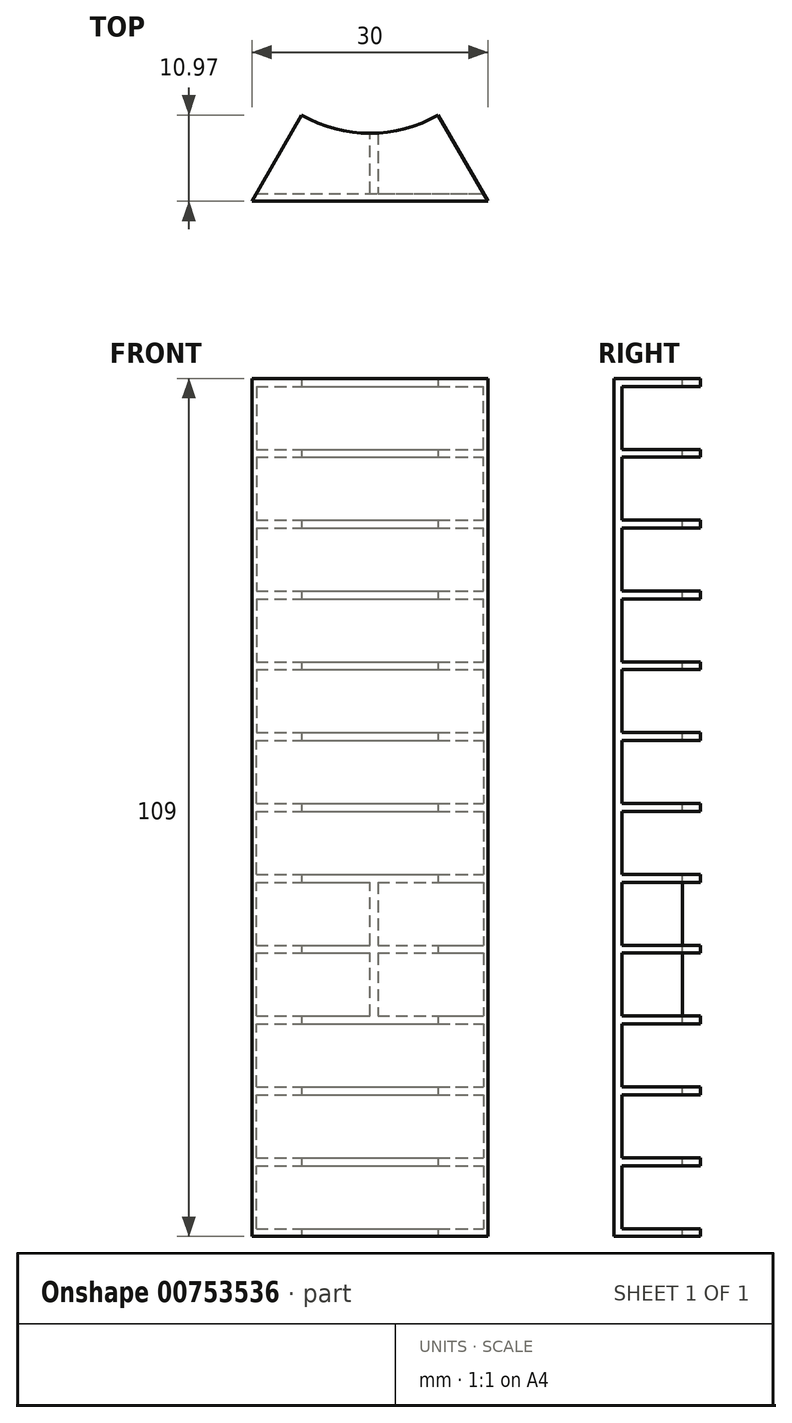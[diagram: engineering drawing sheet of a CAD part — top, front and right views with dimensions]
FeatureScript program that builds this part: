
annotation { "Feature Type Name" : "Feature", "Feature Type Description" : "" }
export const myFeature = defineFeature(function(context is Context, id is Id, definition is map)
    precondition{}
    {
        {
            var Q0;
            Q0=qCreatedBy(makeId("Top.planeOp"),FACE);
            var sketch = newSketch(context, id + "F0", { "sketchPlane" : qUnion([Q0])});
            skCircle(sketch, "E0", {"center": v(0, 0) * mm, "radius": 30 * mm});
            skCircle(sketch, "E1.cCircle", {"center": v(0, 0) * mm, "radius": 30 * mm, "construction": true});
            skLineSegment(sketch, "E1.0", {"start": v(30, 0) * mm, "end": v(15, -25.98) * mm});
            skLineSegment(sketch, "E1.1", {"start": v(15, -25.98) * mm, "end": v(-15, -25.98) * mm});
            skLineSegment(sketch, "E1.2", {"start": v(-15, -25.98) * mm, "end": v(-30, 0) * mm});
            skLineSegment(sketch, "E1.3", {"start": v(-30, 0) * mm, "end": v(-15, 25.98) * mm});
            skLineSegment(sketch, "E1.4", {"start": v(-15, 25.98) * mm, "end": v(15, 25.98) * mm});
            skLineSegment(sketch, "E1.5", {"start": v(15, 25.98) * mm, "end": v(30, 0) * mm});
            skLineSegment(sketch, "E2", {"start": v(-30, 0) * mm, "end": v(30, 0) * mm});
            skLineSegment(sketch, "E3", {"start": v(-15, 25.98) * mm, "end": v(15, -25.98) * mm});
            skLineSegment(sketch, "E4", {"start": v(-15, -25.98) * mm, "end": v(15, 25.98) * mm});
            skCircle(sketch, "E5", {"center": v(0, 0) * mm, "radius": 17.33 * mm});
            skLineSegment(sketch, "E6.0", {"start": v(30, 17.32) * mm, "end": v(30, -17.32) * mm, "construction": true});
            skLineSegment(sketch, "E6.1", {"start": v(30, -17.32) * mm, "end": v(0, -34.64) * mm, "construction": true});
            skLineSegment(sketch, "E6.2", {"start": v(0, -34.64) * mm, "end": v(-30, -17.32) * mm, "construction": true});
            skLineSegment(sketch, "E6.3", {"start": v(-30, -17.32) * mm, "end": v(-30, 17.32) * mm, "construction": true});
            skLineSegment(sketch, "E6.4", {"start": v(-30, 17.32) * mm, "end": v(0, 34.64) * mm, "construction": true});
            skLineSegment(sketch, "E6.5", {"start": v(0, 34.64) * mm, "end": v(30, 17.32) * mm, "construction": true});
            skPoint(sketch, "E6.0.midPoint", {"position": v(30, 0) * mm});
            skLineSegment(sketch, "E7", {"start": v(-30, 17.32) * mm, "end": v(30, -17.32) * mm});
            skLineSegment(sketch, "E8", {"start": v(-30, -17.32) * mm, "end": v(30, 17.32) * mm});
            skLineSegment(sketch, "E9", {"start": v(0, 34.64) * mm, "end": v(0, -34.64) * mm});
            skLineSegment(sketch, "E10", {"start": v(-15, 25.98) * mm, "end": v(55.88, 25.98) * mm, "construction": true});
            skLineSegment(sketch, "E11.0", {"start": v(-14.13, -26.48) * mm, "end": v(15.87, 25.48) * mm});
            skLineSegment(sketch, "E12.0", {"start": v(1, 34.64) * mm, "end": v(1, -34.64) * mm});
            skLineSegment(sketch, "E13", {"start": v(15, -8.67) * mm, "end": v(17.33, 0) * mm});
            skLineSegment(sketch, "E14", {"start": v(-7.78, -15.48) * mm, "end": v(0, -17.33) * mm});
            skSolve(sketch);
        }
        {
            var Q0;
            {var subQ0=sQuery(id+"F0.wireOp",EDGE,"E4");var subQ5=sQuery(id+"F0.wireOp",EDGE,"E5");var subQ6=makeQuery(id+"F0.imprint","INTERSECT",VERTEX,{"disambiguationData":[OD(0.0)],"derivedFrom":[subQ0,subQ5]});Q0=makeQuery(id+"F0.imprint","IMPRINT",FACE,{"disambiguationData":[TD([[makeQuery(id+"F0.imprint","IMPRINT",EDGE,{"disambiguationData":[TD([[subQ6,-1.0]])],"derivedFrom":subQ5}),-1.0]])]});}
            var Q1;
            {var subQ0=sQuery(id+"F0.wireOp",EDGE,"E9");var subQ1=sQuery(id+"F0.wireOp",EDGE,"E1.1");var subQ2=makeQuery(id+"F0.imprint","INTERSECT",VERTEX,{"derivedFrom":[subQ1,subQ0]});Q1=makeQuery(id+"F0.imprint","IMPRINT",FACE,{"disambiguationData":[TD([[makeQuery(id+"F0.imprint","IMPRINT",EDGE,{"disambiguationData":[TD([[subQ2,-1.0]])],"derivedFrom":subQ1}),-1.0]])]});}
            var Q2;
            {var subQ0=sQuery(id+"F0.wireOp",EDGE,"E12.0");var subQ1=sQuery(id+"F0.wireOp",EDGE,"E1.1");var subQ2=makeQuery(id+"F0.imprint","INTERSECT",VERTEX,{"derivedFrom":[subQ1,subQ0]});Q2=makeQuery(id+"F0.imprint","IMPRINT",FACE,{"disambiguationData":[TD([[makeQuery(id+"F0.imprint","IMPRINT",EDGE,{"disambiguationData":[TD([[subQ2,-1.0]])],"derivedFrom":subQ1}),-1.0]])]});}
            var Q3;
            {var subQ0=sQuery(id+"F0.wireOp",EDGE,"E3");var subQ5=sQuery(id+"F0.wireOp",EDGE,"E5");var subQ6=makeQuery(id+"F0.imprint","INTERSECT",VERTEX,{"disambiguationData":[OD(1.0)],"derivedFrom":[subQ0,subQ5]});Q3=makeQuery(id+"F0.imprint","IMPRINT",FACE,{"disambiguationData":[TD([[makeQuery(id+"F0.imprint","IMPRINT",EDGE,{"disambiguationData":[TD([[subQ6,1.0]])],"derivedFrom":subQ5}),-1.0]])]});}
            extrude(context, id + "F1", {"entities" : qUnion([Q0, Q1, Q2, Q3]), "endBound" : BoundingType.SYMMETRIC, "depth" : 109 * mm, "offsetDistance" : 25 * mm});
        }
        {
            var Q0;
            Q0=qCreatedBy(makeId("Right.planeOp"),FACE);
            var sketch = newSketch(context, id + "F2", { "sketchPlane" : qUnion([Q0])});
            skLineSegment(sketch, "E15.bottom", {"start": v(-13.98, 8.5) * mm, "end": v(-24.98, 8.5) * mm});
            skLineSegment(sketch, "E15.top", {"start": v(-13.98, 0.5) * mm, "end": v(-24.98, 0.5) * mm});
            skLineSegment(sketch, "E15.left", {"start": v(-13.98, 8.5) * mm, "end": v(-13.98, 0.5) * mm});
            skLineSegment(sketch, "E15.right", {"start": v(-24.98, 8.5) * mm, "end": v(-24.98, 0.5) * mm});
            skLineSegment(sketch, "E16", {"start": v(46.6, 0) * mm, "end": v(-52.23, 0) * mm, "construction": true});
            skLineSegment(sketch, "E17", {"start": v(-24.98, 77.06) * mm, "end": v(-24.98, -67.63) * mm, "construction": true});
            skLineSegment(sketch, "E18.bottom", {"start": v(-13.98, 9.5) * mm, "end": v(-24.98, 9.5) * mm});
            skLineSegment(sketch, "E18.top", {"start": v(-13.98, 17.5) * mm, "end": v(-24.98, 17.5) * mm});
            skLineSegment(sketch, "E18.left", {"start": v(-13.98, 9.5) * mm, "end": v(-13.98, 17.5) * mm});
            skLineSegment(sketch, "E18.right", {"start": v(-24.98, 9.5) * mm, "end": v(-24.98, 17.5) * mm});
            skLineSegment(sketch, "E19.bottom", {"start": v(-13.98, 18.5) * mm, "end": v(-24.98, 18.5) * mm});
            skLineSegment(sketch, "E19.top", {"start": v(-13.98, 26.5) * mm, "end": v(-24.98, 26.5) * mm});
            skLineSegment(sketch, "E19.left", {"start": v(-13.98, 18.5) * mm, "end": v(-13.98, 26.5) * mm});
            skLineSegment(sketch, "E19.right", {"start": v(-24.98, 18.5) * mm, "end": v(-24.98, 26.5) * mm});
            skLineSegment(sketch, "E20.bottom", {"start": v(-13.98, 27.5) * mm, "end": v(-24.98, 27.5) * mm});
            skLineSegment(sketch, "E20.top", {"start": v(-13.98, 35.5) * mm, "end": v(-24.98, 35.5) * mm});
            skLineSegment(sketch, "E20.left", {"start": v(-13.98, 27.5) * mm, "end": v(-13.98, 35.5) * mm});
            skLineSegment(sketch, "E20.right", {"start": v(-24.98, 27.5) * mm, "end": v(-24.98, 35.5) * mm});
            skLineSegment(sketch, "E21.bottom", {"start": v(-13.98, 36.5) * mm, "end": v(-24.98, 36.5) * mm});
            skLineSegment(sketch, "E21.top", {"start": v(-13.98, 44.5) * mm, "end": v(-24.98, 44.5) * mm});
            skLineSegment(sketch, "E21.left", {"start": v(-13.98, 36.5) * mm, "end": v(-13.98, 44.5) * mm});
            skLineSegment(sketch, "E21.right", {"start": v(-24.98, 36.5) * mm, "end": v(-24.98, 44.5) * mm});
            skLineSegment(sketch, "E22.bottom", {"start": v(-13.98, 45.5) * mm, "end": v(-24.98, 45.5) * mm});
            skLineSegment(sketch, "E22.top", {"start": v(-13.98, 53.5) * mm, "end": v(-24.98, 53.5) * mm});
            skLineSegment(sketch, "E22.left", {"start": v(-13.98, 45.5) * mm, "end": v(-13.98, 53.5) * mm});
            skLineSegment(sketch, "E22.right", {"start": v(-24.98, 45.5) * mm, "end": v(-24.98, 53.5) * mm});
            skLineSegment(sketch, "E23.bottom", {"start": v(-13.98, -0.5) * mm, "end": v(-24.98, -0.5) * mm});
            skLineSegment(sketch, "E23.top", {"start": v(-13.98, -8.5) * mm, "end": v(-24.98, -8.5) * mm});
            skLineSegment(sketch, "E23.left", {"start": v(-13.98, -0.5) * mm, "end": v(-13.98, -8.5) * mm});
            skLineSegment(sketch, "E23.right", {"start": v(-24.98, -0.5) * mm, "end": v(-24.98, -8.5) * mm});
            skLineSegment(sketch, "E24.bottom", {"start": v(-13.98, -9.5) * mm, "end": v(-24.98, -9.5) * mm});
            skLineSegment(sketch, "E24.top", {"start": v(-13.98, -17.5) * mm, "end": v(-24.98, -17.5) * mm});
            skLineSegment(sketch, "E24.left", {"start": v(-13.98, -9.5) * mm, "end": v(-13.98, -17.5) * mm});
            skLineSegment(sketch, "E24.right", {"start": v(-24.98, -9.5) * mm, "end": v(-24.98, -17.5) * mm});
            skLineSegment(sketch, "E25.bottom", {"start": v(-13.98, -18.5) * mm, "end": v(-24.98, -18.5) * mm});
            skLineSegment(sketch, "E25.top", {"start": v(-13.98, -26.5) * mm, "end": v(-24.98, -26.5) * mm});
            skLineSegment(sketch, "E25.left", {"start": v(-13.98, -18.5) * mm, "end": v(-13.98, -26.5) * mm});
            skLineSegment(sketch, "E25.right", {"start": v(-24.98, -18.5) * mm, "end": v(-24.98, -26.5) * mm});
            skLineSegment(sketch, "E26.bottom", {"start": v(-13.98, -27.5) * mm, "end": v(-24.98, -27.5) * mm});
            skLineSegment(sketch, "E26.top", {"start": v(-13.98, -35.5) * mm, "end": v(-24.98, -35.5) * mm});
            skLineSegment(sketch, "E26.left", {"start": v(-13.98, -27.5) * mm, "end": v(-13.98, -35.5) * mm});
            skLineSegment(sketch, "E26.right", {"start": v(-24.98, -27.5) * mm, "end": v(-24.98, -35.5) * mm});
            skLineSegment(sketch, "E27.bottom", {"start": v(-13.98, -36.5) * mm, "end": v(-24.98, -36.5) * mm});
            skLineSegment(sketch, "E27.top", {"start": v(-13.98, -44.5) * mm, "end": v(-24.98, -44.5) * mm});
            skLineSegment(sketch, "E27.left", {"start": v(-13.98, -36.5) * mm, "end": v(-13.98, -44.5) * mm});
            skLineSegment(sketch, "E27.right", {"start": v(-24.98, -36.5) * mm, "end": v(-24.98, -44.5) * mm});
            skLineSegment(sketch, "E28.bottom", {"start": v(-13.98, -45.5) * mm, "end": v(-24.98, -45.5) * mm});
            skLineSegment(sketch, "E28.top", {"start": v(-13.98, -53.5) * mm, "end": v(-24.98, -53.5) * mm});
            skLineSegment(sketch, "E28.left", {"start": v(-13.98, -45.5) * mm, "end": v(-13.98, -53.5) * mm});
            skLineSegment(sketch, "E28.right", {"start": v(-24.98, -45.5) * mm, "end": v(-24.98, -53.5) * mm});
            skSolve(sketch);
        }
        {
            var Q0;
            Q0=makeQuery(id+"F2.imprint","IMPRINT",FACE,{"disambiguationData":[TD([[makeQuery(id+"F2.imprint","IMPRINT",EDGE,{"derivedFrom":sQuery(id+"F2.wireOp",EDGE,"E22.bottom")}),-1.0]])]});
            var Q1;
            Q1=makeQuery(id+"F2.imprint","IMPRINT",FACE,{"disambiguationData":[TD([[makeQuery(id+"F2.imprint","IMPRINT",EDGE,{"derivedFrom":sQuery(id+"F2.wireOp",EDGE,"E21.bottom")}),-1.0]])]});
            var Q2;
            Q2=makeQuery(id+"F2.imprint","IMPRINT",FACE,{"disambiguationData":[TD([[makeQuery(id+"F2.imprint","IMPRINT",EDGE,{"derivedFrom":sQuery(id+"F2.wireOp",EDGE,"E20.bottom")}),-1.0]])]});
            var Q3;
            Q3=makeQuery(id+"F2.imprint","IMPRINT",FACE,{"disambiguationData":[TD([[makeQuery(id+"F2.imprint","IMPRINT",EDGE,{"derivedFrom":sQuery(id+"F2.wireOp",EDGE,"E19.bottom")}),-1.0]])]});
            var Q4;
            Q4=makeQuery(id+"F2.imprint","IMPRINT",FACE,{"disambiguationData":[TD([[makeQuery(id+"F2.imprint","IMPRINT",EDGE,{"derivedFrom":sQuery(id+"F2.wireOp",EDGE,"E18.bottom")}),-1.0]])]});
            var Q5;
            Q5=makeQuery(id+"F2.imprint","IMPRINT",FACE,{"disambiguationData":[TD([[makeQuery(id+"F2.imprint","IMPRINT",EDGE,{"derivedFrom":sQuery(id+"F2.wireOp",EDGE,"E15.bottom")}),1.0]])]});
            var Q6;
            Q6=makeQuery(id+"F2.imprint","IMPRINT",FACE,{"disambiguationData":[TD([[makeQuery(id+"F2.imprint","IMPRINT",EDGE,{"derivedFrom":sQuery(id+"F2.wireOp",EDGE,"E23.bottom")}),1.0]])]});
            var Q7;
            Q7=makeQuery(id+"F2.imprint","IMPRINT",FACE,{"disambiguationData":[TD([[makeQuery(id+"F2.imprint","IMPRINT",EDGE,{"derivedFrom":sQuery(id+"F2.wireOp",EDGE,"E24.bottom")}),1.0]])]});
            var Q8;
            Q8=makeQuery(id+"F2.imprint","IMPRINT",FACE,{"disambiguationData":[TD([[makeQuery(id+"F2.imprint","IMPRINT",EDGE,{"derivedFrom":sQuery(id+"F2.wireOp",EDGE,"E25.bottom")}),1.0]])]});
            var Q9;
            Q9=makeQuery(id+"F2.imprint","IMPRINT",FACE,{"disambiguationData":[TD([[makeQuery(id+"F2.imprint","IMPRINT",EDGE,{"derivedFrom":sQuery(id+"F2.wireOp",EDGE,"E26.bottom")}),1.0]])]});
            var Q10;
            Q10=makeQuery(id+"F2.imprint","IMPRINT",FACE,{"disambiguationData":[TD([[makeQuery(id+"F2.imprint","IMPRINT",EDGE,{"derivedFrom":sQuery(id+"F2.wireOp",EDGE,"E27.bottom")}),1.0]])]});
            var Q11;
            Q11=makeQuery(id+"F2.imprint","IMPRINT",FACE,{"disambiguationData":[TD([[makeQuery(id+"F2.imprint","IMPRINT",EDGE,{"derivedFrom":sQuery(id+"F2.wireOp",EDGE,"E28.bottom")}),1.0]])]});
            extrude(context, id + "F3", {"entities" : qUnion([Q0, Q1, Q2, Q3, Q4, Q5, Q6, Q7, Q8, Q9, Q10, Q11]), "operationType" : NewBodyOperationType.REMOVE, "endBound" : BoundingType.SYMMETRIC, "oppositeDirection" : true, "depth" : 35 * mm, "offsetDistance" : 25 * mm});
        }
        {
            var Q0;
            {var subQ0=sQuery(id+"F0.wireOp",EDGE,"E12.0");var subQ1=sQuery(id+"F0.wireOp",EDGE,"E1.1");var subQ2=makeQuery(id+"F0.imprint","INTERSECT",VERTEX,{"derivedFrom":[subQ1,subQ0]});Q0=makeQuery(id+"F0.imprint","IMPRINT",FACE,{"disambiguationData":[TD([[makeQuery(id+"F0.imprint","IMPRINT",EDGE,{"disambiguationData":[TD([[subQ2,-1.0]])],"derivedFrom":subQ1}),-1.0]])]});}
            var Q1;
            Q1=makeQuery(id+"F3.boolean.opBoolean","COPY",FACE,{"derivedFrom":makeQuery(id+"F3.opExtrude","SWEPT_FACE",FACE,{"disambiguationData":[OSD([sQuery(id+"F2.wireOp",EDGE,"E24.bottom")])]})});
            var Q2;
            Q2=makeQuery(id+"F3.boolean.opBoolean","COPY",FACE,{"derivedFrom":makeQuery(id+"F3.opExtrude","SWEPT_FACE",FACE,{"disambiguationData":[OSD([sQuery(id+"F2.wireOp",EDGE,"E24.bottom")])]})});
            extrude(context, id + "F4", {"entities" : qUnion([Q0]), "operationType" : NewBodyOperationType.ADD, "oppositeDirection" : true, "depth" : 27.2 * mm, "endBoundEntityFace" : qUnion([Q1]), "offsetDistance" : 25 * mm, "hasSecondDirection" : true, "secondDirectionBound" : SecondDirectionBoundingType.UP_TO_SURFACE, "secondDirectionOppositeDirection" : true, "secondDirectionDepth" : 25 * mm, "secondDirectionBoundEntityFace" : qUnion([Q2])});
        }
    });
